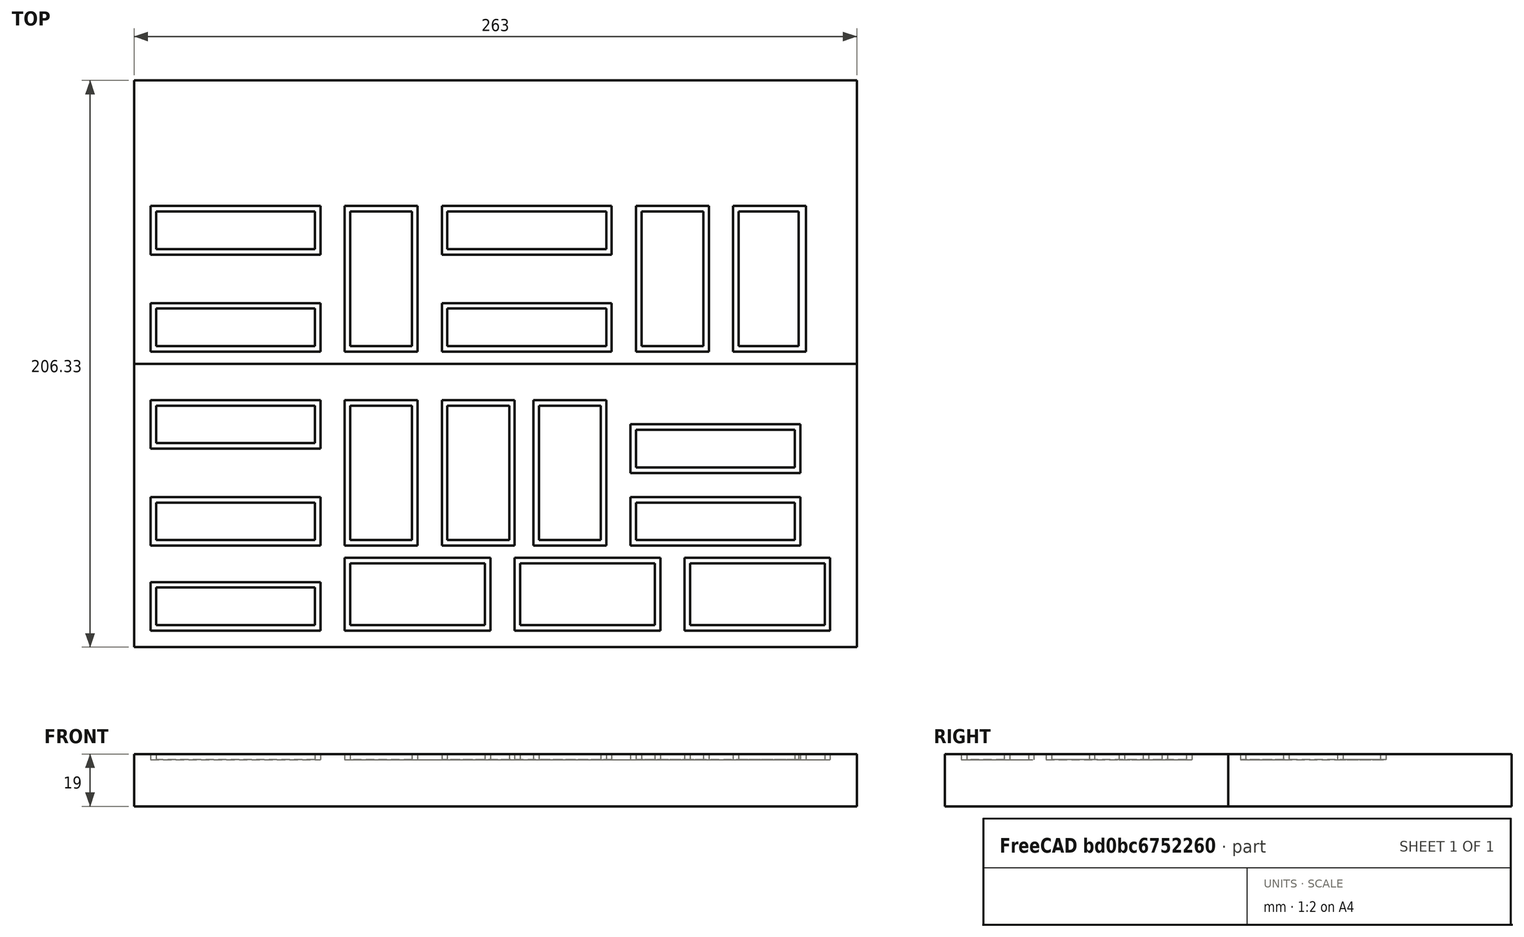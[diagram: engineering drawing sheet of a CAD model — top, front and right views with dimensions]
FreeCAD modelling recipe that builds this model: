
FCSTD DOCUMENT  (FreeCAD 0.22R36958 (Git))
Label: juel_top_3
License: All rights reserved
LicenseURL: http://en.wikipedia.org/wiki/All_rights_reserved
objects: Part::Part2DObjectPython×25, Sketcher::SketchObject×3, PartDesign::Pocket×2, Spreadsheet::Sheet×1, PartDesign::Pad×1, PartDesign::Body×1
note: 35 computed .brp shape members not serialized (recipe doc carries the construction recipe); baked Part::Feature solids carry a one-line shape summary decoded from their .brp

FEATURE [Spreadsheet::Sheet] Spreadsheet  label="vars"
  cells = A1='length; B1(length)=263; C1=263; A2='width; B2(width)==border_size + plot8 * 3 + space_wide + space_narrow * 3; C2=158; A3='height; B3(height)=19; A4='border_size; B4(border_size)=6; A5='cut_height; B5(cut_height)=2; A7='plot10; B7(plot10)==C7 / 20; C7=530; D7=1; A8='plot20; B8(plot20)==C7 / 10; C8=50; D8==200 / E8; E8=5; A9='plot8; B9(plot8)==plot20 / 3; A10='plot25; B10(plot25)==plot10 * 2 + space_narrow; A12='plot border; B12(plot_border)=2; A13='space narrow; B13(space_narrow)==space_wide / 2; A14='space wide; B14(space_wide)==plot20 / 3; A16='font size; B16(font_size)=9.5; A17='x bottom row; B17(x_bottom_row)=-94
FEATURE [Sketcher::SketchObject] Sketch
  AttachmentSupport = -> [XY_Plane]
  FullyConstrained = true
  MapMode = 5
  expr: Constraints[20] = <<vars>>.width
  expr: Constraints[8] = <<vars>>.width
  expr: Constraints[9] = <<vars>>.length
  sketch-geometry (8):
    g0: LineSegment StartX=-131.5 StartY=0 StartZ=0 EndX=131.5 EndY=0 EndZ=0
    g1: LineSegment StartX=131.5 StartY=0 StartZ=0 EndX=131.5 EndY=103.167 EndZ=0
    g2: LineSegment StartX=131.5 StartY=103.167 StartZ=0 EndX=-131.5 EndY=103.167 EndZ=0
    g3: LineSegment StartX=-131.5 StartY=103.167 StartZ=0 EndX=-131.5 EndY=0 EndZ=0
    g4: LineSegment StartX=-131.5 StartY=103.167 StartZ=0 EndX=131.5 EndY=103.167 EndZ=0
    g5: LineSegment StartX=131.5 StartY=103.167 StartZ=0 EndX=131.5 EndY=206.333 EndZ=0
    g6: LineSegment StartX=131.5 StartY=206.333 StartZ=0 EndX=-131.5 EndY=206.333 EndZ=0
    g7: LineSegment StartX=-131.5 StartY=206.333 StartZ=0 EndX=-131.5 EndY=103.167 EndZ=0
  constraints (21):
    c: Coincident(g0,g1)
    c: Coincident(g1,g2)
    c: Coincident(g2,g3)
    c: Coincident(g3,g0)
    c: Horizontal(g0)
    c: Horizontal(g2)
    c: Vertical(g1)
    c: Vertical(g3)
    c: DistanceY(g3,g3) = 103.167
    c: DistanceX(g2,g2) = 263
    c: Symmetric(g0,g0,g-1)
    c: Coincident(g4,g5)
    c: Coincident(g5,g6)
    c: Coincident(g6,g7)
    c: Coincident(g7,g4)
    c: Horizontal(g6)
    c: Vertical(g5)
    c: Vertical(g7)
    c: Coincident(g4,g2)
    c: Coincident(g1,g4)
    c: DistanceY(g7,g7) = 103.167
FEATURE [PartDesign::Pad] Pad
  Direction = (0,0,1)
  Length = 19
  Length2 = 10
  Profile = -> Sketch
  ReferenceAxis = -> Sketch [N_Axis]
  Suppressed = false
  Type = 0
  expr: Length = <<vars>>.height
FEATURE [Sketcher::SketchObject] Sketch001
  AttachmentSupport = -> [Pad]
  ExternalGeometry = -> [Pad]
  FullyConstrained = true
  MapMode = 5
  Placement = pos=(0,0,19) rot=(0,0,1;0rad)
  expr: Constraints[142] = <<vars>>.space_narrow
  expr: Constraints[143] = <<vars>>.space_narrow
  expr: Constraints[144] = <<vars>>.space_narrow
  expr: Constraints[161] = <<vars>>.plot_border
  expr: Constraints[162] = <<vars>>.plot_border
  expr: Constraints[163] = <<vars>>.plot10
  expr: Constraints[164] = <<vars>>.plot_border
  expr: Constraints[165] = <<vars>>.plot_border
  expr: Constraints[166] = <<vars>>.plot20
  expr: Constraints[16] = <<vars>>.plot_border
  expr: Constraints[17] = <<vars>>.plot_border
  expr: Constraints[18] = <<vars>>.plot_border
  expr: Constraints[19] = <<vars>>.plot_border
  expr: Constraints[20] = <<vars>>.plot8
  expr: Constraints[214] = <<vars>>.space_narrow - 2
  expr: Constraints[21] = <<vars>>.plot25
  expr: Constraints[249] = <<vars>>.plot_border
  expr: Constraints[250] = <<vars>>.plot_border
  expr: Constraints[251] = <<vars>>.plot_border
  expr: Constraints[252] = <<vars>>.plot_border
  expr: Constraints[253] = <<vars>>.plot25
  expr: Constraints[254] = <<vars>>.plot25
  expr: Constraints[255] = <<vars>>.plot_border
  expr: Constraints[256] = <<vars>>.plot_border
  expr: Constraints[257] = <<vars>>.plot_border
  expr: Constraints[258] = <<vars>>.plot_border
  expr: Constraints[259] = <<vars>>.plot8
  expr: Constraints[260] = <<vars>>.plot8
  expr: Constraints[263] = <<vars>>.space_narrow
  expr: Constraints[264] = <<vars>>.space_narrow
  expr: Constraints[68] = <<vars>>.border_size
  expr: Constraints[70] = <<vars>>.space_narrow * 1.5
  expr: Constraints[71] = <<vars>>.space_wide
  expr: Constraints[72] = <<vars>>.border_size
  expr: Constraints[89] = <<vars>>.plot_border
  expr: Constraints[90] = <<vars>>.plot_border
  expr: Constraints[91] = <<vars>>.plot_border
  expr: Constraints[92] = <<vars>>.plot_border
  expr: Constraints[93] = <<vars>>.plot10
  expr: Constraints[94] = <<vars>>.plot20
  sketch-geometry (88):
    g0: LineSegment StartX=-125.5 StartY=6 StartZ=0 EndX=-63.6667 EndY=6 EndZ=0
    g1: LineSegment StartX=-63.6667 StartY=6 StartZ=0 EndX=-63.6667 EndY=23.6667 EndZ=0
    g2: LineSegment StartX=-63.6667 StartY=23.6667 StartZ=0 EndX=-125.5 EndY=23.6667 EndZ=0
    g3: LineSegment StartX=-125.5 StartY=23.6667 StartZ=0 EndX=-125.5 EndY=6 EndZ=0
    g4: LineSegment StartX=-65.6667 StartY=21.6667 StartZ=0 EndX=-123.5 EndY=21.6667 EndZ=0
    g5: LineSegment StartX=-123.5 StartY=21.6667 StartZ=0 EndX=-123.5 EndY=8 EndZ=0
    g6: LineSegment StartX=-123.5 StartY=8 StartZ=0 EndX=-65.6667 EndY=8 EndZ=0
    g7: LineSegment StartX=-65.6667 StartY=8 StartZ=0 EndX=-65.6667 EndY=21.6667 EndZ=0
    g8: LineSegment StartX=-125.5 StartY=36.9167 StartZ=0 EndX=-63.6667 EndY=36.9167 EndZ=0
    g9: LineSegment StartX=-63.6667 StartY=36.9167 StartZ=0 EndX=-63.6667 EndY=54.5833 EndZ=0
    g10: LineSegment StartX=-63.6667 StartY=54.5833 StartZ=0 EndX=-125.5 EndY=54.5833 EndZ=0
    g11: LineSegment StartX=-125.5 StartY=54.5833 StartZ=0 EndX=-125.5 EndY=36.9167 EndZ=0
    g12: LineSegment StartX=-65.6667 StartY=52.5833 StartZ=0 EndX=-123.5 EndY=52.5833 EndZ=0
    g13: LineSegment StartX=-123.5 StartY=52.5833 StartZ=0 EndX=-123.5 EndY=38.9167 EndZ=0
    g14: LineSegment StartX=-123.5 StartY=38.9167 StartZ=0 EndX=-65.6667 EndY=38.9167 EndZ=0
    g15: LineSegment StartX=-65.6667 StartY=38.9167 StartZ=0 EndX=-65.6667 EndY=52.5833 EndZ=0
    g16: LineSegment StartX=-125.5 StartY=72.25 StartZ=0 EndX=-63.6667 EndY=72.25 EndZ=0
    g17: LineSegment StartX=-63.6667 StartY=72.25 StartZ=0 EndX=-63.6667 EndY=89.9167 EndZ=0
    g18: LineSegment StartX=-63.6667 StartY=89.9167 StartZ=0 EndX=-125.5 EndY=89.9167 EndZ=0
    g19: LineSegment StartX=-125.5 StartY=89.9167 StartZ=0 EndX=-125.5 EndY=72.25 EndZ=0
    g20: LineSegment StartX=-65.6667 StartY=87.9167 StartZ=0 EndX=-123.5 EndY=87.9167 EndZ=0
    g21: LineSegment StartX=-123.5 StartY=87.9167 StartZ=0 EndX=-123.5 EndY=74.25 EndZ=0
    g22: LineSegment StartX=-123.5 StartY=74.25 StartZ=0 EndX=-65.6667 EndY=74.25 EndZ=0
    g23: LineSegment StartX=-65.6667 StartY=74.25 StartZ=0 EndX=-65.6667 EndY=87.9167 EndZ=0
    g24: LineSegment StartX=-54.8333 StartY=6 StartZ=0 EndX=-1.83333 EndY=6 EndZ=0
    g25: LineSegment StartX=-1.83333 StartY=6 StartZ=0 EndX=-1.83333 EndY=32.5 EndZ=0
    g26: LineSegment StartX=-1.83333 StartY=32.5 StartZ=0 EndX=-54.8333 EndY=32.5 EndZ=0
    g27: LineSegment StartX=-54.8333 StartY=32.5 StartZ=0 EndX=-54.8333 EndY=6 EndZ=0
    g28: LineSegment StartX=-52.8333 StartY=8 StartZ=0 EndX=-3.83333 EndY=8 EndZ=0
    g29: LineSegment StartX=-3.83333 StartY=8 StartZ=0 EndX=-3.83333 EndY=30.5 EndZ=0
    g30: LineSegment StartX=-3.83333 StartY=30.5 StartZ=0 EndX=-52.8333 EndY=30.5 EndZ=0
    g31: LineSegment StartX=-52.8333 StartY=30.5 StartZ=0 EndX=-52.8333 EndY=8 EndZ=0
    g32: LineSegment StartX=7 StartY=6 StartZ=0 EndX=60 EndY=6 EndZ=0
    g33: LineSegment StartX=60 StartY=6 StartZ=0 EndX=60 EndY=32.5 EndZ=0
    g34: LineSegment StartX=60 StartY=32.5 StartZ=0 EndX=7 EndY=32.5 EndZ=0
    g35: LineSegment StartX=7 StartY=32.5 StartZ=0 EndX=7 EndY=6 EndZ=0
    g36: LineSegment StartX=9 StartY=8 StartZ=0 EndX=58 EndY=8 EndZ=0
    g37: LineSegment StartX=58 StartY=8 StartZ=0 EndX=58 EndY=30.5 EndZ=0
    g38: LineSegment StartX=58 StartY=30.5 StartZ=0 EndX=9 EndY=30.5 EndZ=0
    g39: LineSegment StartX=9 StartY=30.5 StartZ=0 EndX=9 EndY=8 EndZ=0
    g40: LineSegment StartX=68.8333 StartY=6 StartZ=0 EndX=121.833 EndY=6 EndZ=0
    g41: LineSegment StartX=121.833 StartY=6 StartZ=0 EndX=121.833 EndY=32.5 EndZ=0
    g42: LineSegment StartX=121.833 StartY=32.5 StartZ=0 EndX=68.8333 EndY=32.5 EndZ=0
    g43: LineSegment StartX=68.8333 StartY=32.5 StartZ=0 EndX=68.8333 EndY=6 EndZ=0
    g44: LineSegment StartX=70.8333 StartY=8 StartZ=0 EndX=119.833 EndY=8 EndZ=0
    g45: LineSegment StartX=119.833 StartY=8 StartZ=0 EndX=119.833 EndY=30.5 EndZ=0
    g46: LineSegment StartX=119.833 StartY=30.5 StartZ=0 EndX=70.8333 EndY=30.5 EndZ=0
    g47: LineSegment StartX=70.8333 StartY=30.5 StartZ=0 EndX=70.8333 EndY=8 EndZ=0
    g48: LineSegment StartX=-54.8333 StartY=36.9167 StartZ=0 EndX=-28.3333 EndY=36.9167 EndZ=0
    g49: LineSegment StartX=-28.3333 StartY=36.9167 StartZ=0 EndX=-28.3333 EndY=89.9167 EndZ=0
    g50: LineSegment StartX=-28.3333 StartY=89.9167 StartZ=0 EndX=-54.8333 EndY=89.9167 EndZ=0
    g51: LineSegment StartX=-54.8333 StartY=89.9167 StartZ=0 EndX=-54.8333 EndY=36.9167 EndZ=0
    g52: LineSegment StartX=-30.3333 StartY=87.9167 StartZ=0 EndX=-52.8333 EndY=87.9167 EndZ=0
    g53: LineSegment StartX=-52.8333 StartY=87.9167 StartZ=0 EndX=-52.8333 EndY=38.9167 EndZ=0
    g54: LineSegment StartX=-52.8333 StartY=38.9167 StartZ=0 EndX=-30.3333 EndY=38.9167 EndZ=0
    g55: LineSegment StartX=-30.3333 StartY=38.9167 StartZ=0 EndX=-30.3333 EndY=87.9167 EndZ=0
    g56: LineSegment StartX=-19.5 StartY=36.9167 StartZ=0 EndX=7 EndY=36.9167 EndZ=0
    g57: LineSegment StartX=7 StartY=36.9167 StartZ=0 EndX=7 EndY=89.9167 EndZ=0
    g58: LineSegment StartX=7 StartY=89.9167 StartZ=0 EndX=-19.5 EndY=89.9167 EndZ=0
    g59: LineSegment StartX=-19.5 StartY=89.9167 StartZ=0 EndX=-19.5 EndY=36.9167 EndZ=0
    g60: LineSegment StartX=5 StartY=87.9167 StartZ=0 EndX=-17.5 EndY=87.9167 EndZ=0
    g61: LineSegment StartX=-17.5 StartY=87.9167 StartZ=0 EndX=-17.5 EndY=38.9167 EndZ=0
    g62: LineSegment StartX=-17.5 StartY=38.9167 StartZ=0 EndX=5 EndY=38.9167 EndZ=0
    g63: LineSegment StartX=5 StartY=38.9167 StartZ=0 EndX=5 EndY=87.9167 EndZ=0
    g64: LineSegment StartX=13.8333 StartY=36.9167 StartZ=0 EndX=40.3333 EndY=36.9167 EndZ=0
    g65: LineSegment StartX=40.3333 StartY=36.9167 StartZ=0 EndX=40.3333 EndY=89.9167 EndZ=0
    g66: LineSegment StartX=40.3333 StartY=89.9167 StartZ=0 EndX=13.8333 EndY=89.9167 EndZ=0
    g67: LineSegment StartX=13.8333 StartY=89.9167 StartZ=0 EndX=13.8333 EndY=36.9167 EndZ=0
    g68: LineSegment StartX=38.3333 StartY=87.9167 StartZ=0 EndX=15.8333 EndY=87.9167 EndZ=0
    g69: LineSegment StartX=15.8333 StartY=87.9167 StartZ=0 EndX=15.8333 EndY=38.9167 EndZ=0
    g70: LineSegment StartX=15.8333 StartY=38.9167 StartZ=0 EndX=38.3333 EndY=38.9167 EndZ=0
    g71: LineSegment StartX=38.3333 StartY=38.9167 StartZ=0 EndX=38.3333 EndY=87.9167 EndZ=0
    g72: LineSegment StartX=49.1667 StartY=36.9167 StartZ=0 EndX=111 EndY=36.9167 EndZ=0
    g73: LineSegment StartX=111 StartY=36.9167 StartZ=0 EndX=111 EndY=54.5833 EndZ=0
    g74: LineSegment StartX=111 StartY=54.5833 StartZ=0 EndX=49.1667 EndY=54.5833 EndZ=0
    g75: LineSegment StartX=49.1667 StartY=54.5833 StartZ=0 EndX=49.1667 EndY=36.9167 EndZ=0
    g76: LineSegment StartX=109 StartY=52.5833 StartZ=0 EndX=51.1667 EndY=52.5833 EndZ=0
    g77: LineSegment StartX=51.1667 StartY=52.5833 StartZ=0 EndX=51.1667 EndY=38.9167 EndZ=0
    g78: LineSegment StartX=51.1667 StartY=38.9167 StartZ=0 EndX=109 EndY=38.9167 EndZ=0
    g79: LineSegment StartX=109 StartY=38.9167 StartZ=0 EndX=109 EndY=52.5833 EndZ=0
    g80: LineSegment StartX=49.1667 StartY=63.4167 StartZ=0 EndX=111 EndY=63.4167 EndZ=0
    g81: LineSegment StartX=111 StartY=63.4167 StartZ=0 EndX=111 EndY=81.0833 EndZ=0
    g82: LineSegment StartX=111 StartY=81.0833 StartZ=0 EndX=49.1667 EndY=81.0833 EndZ=0
    g83: LineSegment StartX=49.1667 StartY=81.0833 StartZ=0 EndX=49.1667 EndY=63.4167 EndZ=0
    g84: LineSegment StartX=109 StartY=79.0833 StartZ=0 EndX=51.1667 EndY=79.0833 EndZ=0
    g85: LineSegment StartX=51.1667 StartY=79.0833 StartZ=0 EndX=51.1667 EndY=65.4167 EndZ=0
    g86: LineSegment StartX=51.1667 StartY=65.4167 StartZ=0 EndX=109 EndY=65.4167 EndZ=0
    g87: LineSegment StartX=109 StartY=65.4167 StartZ=0 EndX=109 EndY=79.0833 EndZ=0
  constraints (265):
    c: Coincident(g0,g1)
    c: Coincident(g1,g2)
    c: Coincident(g2,g3)
    c: Coincident(g3,g0)
    c: Horizontal(g0)
    c: Horizontal(g2)
    c: Vertical(g1)
    c: Vertical(g3)
    c: Coincident(g4,g5)
    c: Coincident(g5,g6)
    c: Coincident(g6,g7)
    c: Coincident(g7,g4)
    c: Horizontal(g4)
    c: Horizontal(g6)
    c: Vertical(g5)
    c: Vertical(g7)
    c: DistanceX(g2,g4) = 2
    c: DistanceY(g4,g2) = 2
    c: DistanceY(g0,g6) = 2
    c: DistanceX(g6,g0) = 2
    c: DistanceY(g1,g1) = 17.6667
    c: DistanceX(g2,g2) = 61.8333
    c: Coincident(g8,g9)
    c: Coincident(g16,g17)
    c: Coincident(g9,g10)
    c: Coincident(g17,g18)
    c: Coincident(g10,g11)
    c: Coincident(g18,g19)
    c: Coincident(g11,g8)
    c: Coincident(g19,g16)
    c: Horizontal(g8)
    c: Horizontal(g16)
    c: Horizontal(g10)
    c: Horizontal(g18)
    c: Vertical(g9)
    c: Vertical(g17)
    c: Vertical(g11)
    c: Vertical(g19)
    c: Coincident(g12,g13)
    c: Coincident(g20,g21)
    c: Coincident(g13,g14)
    c: Coincident(g21,g22)
    c: Coincident(g14,g15)
    c: Coincident(g22,g23)
    c: Coincident(g15,g12)
    c: Coincident(g23,g20)
    c: Horizontal(g12)
    c: Horizontal(g20)
    c: Horizontal(g14)
    c: Horizontal(g22)
    c: Vertical(g13)
    c: Vertical(g21)
    c: Vertical(g15)
    c: Vertical(g23)
    c: DistanceX(g10,g12) = 2
    c: DistanceX(g18,g20) = 2
    c: DistanceY(g12,g10) = 2
    c: DistanceY(g20,g18) = 2
    c: DistanceY(g8,g14) = 2
    c: DistanceY(g16,g22) = 2
    c: DistanceX(g14,g8) = 2
    c: DistanceX(g22,g16) = 2
    c: Equal(g1,g9)
    c: Equal(g1,g17)
    c: Equal(g2,g10)
    c: Equal(g2,g18)
    c: Vertical(g2,g8)
    c: Vertical(g8,g16)
    c: DistanceY(g-3,g0) = 6
    c: Distance(g-3,g0) = 8.48528
    c: DistanceY(g2,g8) = 13.25
    c: DistanceY(g10,g16) = 17.6667
    c: DistanceX(g-3,g0) = 6
    c: Coincident(g24,g25)
    c: Coincident(g25,g26)
    c: Coincident(g26,g27)
    c: Coincident(g27,g24)
    c: Horizontal(g24)
    c: Horizontal(g26)
    c: Vertical(g25)
    c: Vertical(g27)
    c: Coincident(g28,g29)
    c: Coincident(g29,g30)
    c: Coincident(g30,g31)
    c: Coincident(g31,g28)
    c: Horizontal(g28)
    c: Horizontal(g30)
    c: Vertical(g29)
    c: Vertical(g31)
    c: DistanceX(g26,g30) = 2
    c: DistanceX(g28,g24) = 2
    c: DistanceY(g30,g26) = 2
    c: DistanceY(g24,g28) = 2
    c: DistanceY(g27,g27) = 26.5
    c: DistanceX(g26,g26) = 53
    c: Horizontal(g0,g24)
    c: Coincident(g32,g33)
    c: Coincident(g40,g41)
    c: Coincident(g33,g34)
    c: Coincident(g41,g42)
    c: Coincident(g34,g35)
    c: Coincident(g42,g43)
    c: Coincident(g35,g32)
    c: Coincident(g43,g40)
    c: Horizontal(g32)
    c: Horizontal(g40)
    c: Horizontal(g34)
    c: Horizontal(g42)
    c: Vertical(g33)
    c: Vertical(g41)
    c: Vertical(g35)
    c: Vertical(g43)
    c: Coincident(g36,g37)
    c: Coincident(g44,g45)
    c: Coincident(g37,g38)
    c: Coincident(g45,g46)
    c: Coincident(g38,g39)
    c: Coincident(g46,g47)
    c: Coincident(g39,g36)
    c: Coincident(g47,g44)
    c: Horizontal(g36)
    c: Horizontal(g44)
    c: Horizontal(g38)
    c: Horizontal(g46)
    c: Vertical(g37)
    c: Vertical(g45)
    c: Vertical(g39)
    c: Vertical(g47)
    c: DistanceX(g34,g38) = 2
    c: DistanceX(g42,g46) = 2
    c: DistanceX(g36,g32) = 2
    c: DistanceX(g44,g40) = 2
    c: DistanceY(g38,g34) = 2
    c: DistanceY(g46,g42) = 2
    c: DistanceY(g32,g36) = 2
    c: DistanceY(g40,g44) = 2
    c: Equal(g27,g35)
    c: Equal(g27,g43)
    c: Equal(g26,g34)
    c: Equal(g26,g42)
    c: Horizontal(g24,g32)
    c: Horizontal(g32,g40)
    c: DistanceX(g0,g24) = 8.83333
    c: DistanceX(g24,g32) = 8.83333
    c: DistanceX(g32,g40) = 8.83333
    c: Coincident(g48,g49)
    c: Coincident(g49,g50)
    c: Coincident(g50,g51)
    c: Coincident(g51,g48)
    c: Horizontal(g48)
    c: Horizontal(g50)
    c: Vertical(g49)
    c: Vertical(g51)
    c: Coincident(g52,g53)
    c: Coincident(g53,g54)
    c: Coincident(g54,g55)
    c: Coincident(g55,g52)
    c: Horizontal(g52)
    c: Horizontal(g54)
    c: Vertical(g53)
    c: Vertical(g55)
    c: DistanceX(g50,g52) = 2
    c: DistanceX(g54,g48) = 2
    c: DistanceX(g48,g48) = 26.5
    c: DistanceY(g52,g50) = 2
    c: DistanceY(g48,g54) = 2
    c: DistanceY(g49,g49) = 53
    c: Horizontal(g8,g48)
    c: Coincident(g56,g57)
    c: Coincident(g64,g65)
    c: Coincident(g57,g58)
    c: Coincident(g65,g66)
    c: Coincident(g58,g59)
    c: Coincident(g66,g67)
    c: Coincident(g59,g56)
    c: Coincident(g67,g64)
    c: Horizontal(g56)
    c: Horizontal(g64)
    c: Horizontal(g58)
    c: Horizontal(g66)
    c: Vertical(g57)
    c: Vertical(g65)
    c: Vertical(g59)
    c: Vertical(g67)
    c: Coincident(g60,g61)
    c: Coincident(g68,g69)
    c: Coincident(g61,g62)
    c: Coincident(g69,g70)
    c: Coincident(g62,g63)
    c: Coincident(g70,g71)
    c: Coincident(g63,g60)
    c: Coincident(g71,g68)
    c: Horizontal(g60)
    c: Horizontal(g68)
    c: Horizontal(g62)
    c: Horizontal(g70)
    c: Vertical(g61)
    c: Vertical(g69)
    c: Vertical(g63)
    c: Vertical(g71)
    c: DistanceX(g58,g60) = 2
    c: DistanceX(g66,g68) = 2
    c: DistanceX(g62,g56) = 2
    c: DistanceX(g70,g64) = 2
    c: Equal(g48,g56)
    c: Equal(g48,g64)
    c: DistanceY(g60,g58) = 2
    c: DistanceY(g68,g66) = 2
    c: DistanceY(g56,g62) = 2
    c: DistanceY(g64,g70) = 2
    c: Equal(g49,g57)
    c: Equal(g49,g65)
    c: Vertical(g26,g48)
    c: Vertical(g56,g34)
    c: DistanceX(g56,g64) = 6.83333
    c: Horizontal(g48,g56)
    c: Horizontal(g56,g64)
    c: Coincident(g72,g73)
    c: Coincident(g73,g74)
    c: Coincident(g74,g75)
    c: Coincident(g75,g72)
    c: Horizontal(g72)
    c: Horizontal(g74)
    c: Vertical(g73)
    c: Vertical(g75)
    c: Coincident(g76,g77)
    c: Coincident(g77,g78)
    c: Coincident(g78,g79)
    c: Coincident(g79,g76)
    c: Horizontal(g76)
    c: Horizontal(g78)
    c: Vertical(g77)
    c: Vertical(g79)
    c: Coincident(g80,g81)
    c: Coincident(g81,g82)
    c: Coincident(g82,g83)
    c: Coincident(g83,g80)
    c: Horizontal(g80)
    c: Horizontal(g82)
    c: Vertical(g81)
    c: Vertical(g83)
    c: Coincident(g84,g85)
    c: Coincident(g85,g86)
    c: Coincident(g86,g87)
    c: Coincident(g87,g84)
    c: Horizontal(g84)
    c: Horizontal(g86)
    c: Vertical(g85)
    c: Vertical(g87)
    c: DistanceX(g82,g84) = 2
    c: DistanceX(g86,g80) = 2
    c: DistanceX(g74,g76) = 2
    c: DistanceX(g78,g72) = 2
    c: DistanceX(g74,g74) = 61.8333
    c: DistanceX(g82,g82) = 61.8333
    c: DistanceY(g84,g82) = 2
    c: DistanceY(g80,g86) = 2
    c: DistanceY(g76,g74) = 2
    c: DistanceY(g72,g78) = 2
    c: DistanceY(g73,g73) = 17.6667
    c: DistanceY(g81,g81) = 17.6667
    c: Vertical(g74,g80)
    c: Horizontal(g64,g72)
    c: DistanceX(g64,g72) = 8.83333
    c: DistanceY(g74,g80) = 8.83333
FEATURE [PartDesign::Pocket] Pocket
  BaseFeature = -> Pad
  Direction = (0,0,-1)
  Length = 2
  Length2 = 5
  Profile = -> Sketch001
  ReferenceAxis = -> Sketch001 [N_Axis]
  Suppressed = false
  Type = 0
  expr: Length = <<vars>>.cut_height
FEATURE [Part::Part2DObjectPython] ShapeString  label="18"  # Draft 2D object (typed FeaturePython)
  FontFile = /System/Library/Fonts/Avenir Next Condensed.ttc
  Fuse = false
  Justification = 4
  JustificationReference = 0
  KeepLeftMargin = false
  MakeFace = true
  ObliqueAngle = 0
  Placement = pos=(-94,14.7,19.01) rot=(0,0,1;4.71239rad)
  ScaleToSize = true
  Size = 9.5
  String = 18
  Tracking = 0
  expr: .Placement.Base.x = <<vars>>.x_bottom_row
  expr: Size = <<vars>>.font_size
FEATURE [Sketcher::SketchObject] Sketch002
  AttachmentSupport = -> [Pocket]
  ExternalGeometry = -> [Pocket]
  FullyConstrained = true
  MapMode = 5
  Placement = pos=(0,0,19) rot=(0,0,1;0rad)
  expr: Constraints[112] = <<vars>>.plot_border
  expr: Constraints[113] = <<vars>>.plot_border
  expr: Constraints[114] = <<vars>>.plot_border
  expr: Constraints[115] = <<vars>>.plot_border
  expr: Constraints[116] = <<vars>>.plot_border
  expr: Constraints[117] = <<vars>>.plot_border
  expr: Constraints[118] = <<vars>>.plot_border
  expr: Constraints[119] = <<vars>>.plot_border
  expr: Constraints[120] = <<vars>>.plot_border
  expr: Constraints[121] = <<vars>>.plot_border
  expr: Constraints[122] = <<vars>>.plot_border
  expr: Constraints[123] = <<vars>>.plot_border
  expr: Constraints[124] = <<vars>>.plot_border
  expr: Constraints[126] = <<vars>>.plot_border
  expr: Constraints[127] = <<vars>>.plot_border
  expr: Constraints[128] = <<vars>>.plot_border
  expr: Constraints[129] = <<vars>>.plot_border
  expr: Constraints[130] = <<vars>>.plot_border
  expr: Constraints[131] = <<vars>>.plot_border
  expr: Constraints[132] = <<vars>>.plot_border
  expr: Constraints[133] = <<vars>>.plot_border
  expr: Constraints[134] = <<vars>>.plot_border
  expr: Constraints[135] = <<vars>>.plot_border
  expr: Constraints[136] = <<vars>>.plot_border
  expr: Constraints[137] = <<vars>>.plot_border
  expr: Constraints[138] = <<vars>>.plot_border
  expr: Constraints[139] = <<vars>>.plot_border
  expr: Constraints[140] = <<vars>>.plot20
  expr: Constraints[141] = <<vars>>.plot20
  expr: Constraints[142] = <<vars>>.plot8
  expr: Constraints[143] = <<vars>>.plot8
  expr: Constraints[144] = <<vars>>.plot20
  expr: Constraints[145] = <<vars>>.plot8
  expr: Constraints[146] = <<vars>>.plot8
  expr: Constraints[147] = <<vars>>.plot25
  expr: Constraints[148] = <<vars>>.plot25
  expr: Constraints[149] = <<vars>>.plot10
  expr: Constraints[150] = <<vars>>.plot25
  expr: Constraints[151] = <<vars>>.plot25
  expr: Constraints[152] = <<vars>>.plot10
  expr: Constraints[153] = <<vars>>.plot10
  expr: Constraints[154] = <<vars>>.space_narrow / 2
  expr: Constraints[155] = <<vars>>.border_size
  expr: Constraints[164] = <<vars>>.space_narrow
  expr: Constraints[165] = <<vars>>.space_narrow
  expr: Constraints[166] = <<vars>>.space_narrow
  expr: Constraints[167] = <<vars>>.space_narrow
  sketch-geometry (56):
    g0: LineSegment StartX=-125.5 StartY=107.583 StartZ=0 EndX=-63.6667 EndY=107.583 EndZ=0
    g1: LineSegment StartX=-63.6667 StartY=107.583 StartZ=0 EndX=-63.6667 EndY=125.25 EndZ=0
    g2: LineSegment StartX=-63.6667 StartY=125.25 StartZ=0 EndX=-125.5 EndY=125.25 EndZ=0
    g3: LineSegment StartX=-125.5 StartY=125.25 StartZ=0 EndX=-125.5 EndY=107.583 EndZ=0
    g4: LineSegment StartX=-65.6667 StartY=123.25 StartZ=0 EndX=-123.5 EndY=123.25 EndZ=0
    g5: LineSegment StartX=-123.5 StartY=123.25 StartZ=0 EndX=-123.5 EndY=109.583 EndZ=0
    g6: LineSegment StartX=-123.5 StartY=109.583 StartZ=0 EndX=-65.6667 EndY=109.583 EndZ=0
    g7: LineSegment StartX=-65.6667 StartY=109.583 StartZ=0 EndX=-65.6667 EndY=123.25 EndZ=0
    g8: LineSegment StartX=-125.5 StartY=142.917 StartZ=0 EndX=-63.6667 EndY=142.917 EndZ=0
    g9: LineSegment StartX=-63.6667 StartY=142.917 StartZ=0 EndX=-63.6667 EndY=160.583 EndZ=0
    g10: LineSegment StartX=-63.6667 StartY=160.583 StartZ=0 EndX=-125.5 EndY=160.583 EndZ=0
    g11: LineSegment StartX=-125.5 StartY=160.583 StartZ=0 EndX=-125.5 EndY=142.917 EndZ=0
    g12: LineSegment StartX=-65.6667 StartY=158.583 StartZ=0 EndX=-123.5 EndY=158.583 EndZ=0
    g13: LineSegment StartX=-123.5 StartY=158.583 StartZ=0 EndX=-123.5 EndY=144.917 EndZ=0
    g14: LineSegment StartX=-123.5 StartY=144.917 StartZ=0 EndX=-65.6667 EndY=144.917 EndZ=0
    g15: LineSegment StartX=-65.6667 StartY=144.917 StartZ=0 EndX=-65.6667 EndY=158.583 EndZ=0
    g16: LineSegment StartX=-54.8333 StartY=160.583 StartZ=0 EndX=-54.8333 EndY=107.583 EndZ=0
    g17: LineSegment StartX=-54.8333 StartY=107.583 StartZ=0 EndX=-28.3333 EndY=107.583 EndZ=0
    g18: LineSegment StartX=-28.3333 StartY=107.583 StartZ=0 EndX=-28.3333 EndY=160.583 EndZ=0
    g19: LineSegment StartX=-28.3333 StartY=160.583 StartZ=0 EndX=-54.8333 EndY=160.583 EndZ=0
    g20: LineSegment StartX=-30.3333 StartY=109.583 StartZ=0 EndX=-30.3333 EndY=158.583 EndZ=0
    g21: LineSegment StartX=-30.3333 StartY=158.583 StartZ=0 EndX=-52.8333 EndY=158.583 EndZ=0
    g22: LineSegment StartX=-52.8333 StartY=158.583 StartZ=0 EndX=-52.8333 EndY=109.583 EndZ=0
    g23: LineSegment StartX=-52.8333 StartY=109.583 StartZ=0 EndX=-30.3333 EndY=109.583 EndZ=0
    g24: LineSegment StartX=42.3333 StartY=125.25 StartZ=0 EndX=-19.5 EndY=125.25 EndZ=0
    g25: LineSegment StartX=-19.5 StartY=125.25 StartZ=0 EndX=-19.5 EndY=107.583 EndZ=0
    g26: LineSegment StartX=-19.5 StartY=107.583 StartZ=0 EndX=42.3333 EndY=107.583 EndZ=0
    g27: LineSegment StartX=42.3333 StartY=107.583 StartZ=0 EndX=42.3333 EndY=125.25 EndZ=0
    g28: LineSegment StartX=-17.5 StartY=109.583 StartZ=0 EndX=40.3333 EndY=109.583 EndZ=0
    g29: LineSegment StartX=40.3333 StartY=109.583 StartZ=0 EndX=40.3333 EndY=123.25 EndZ=0
    g30: LineSegment StartX=40.3333 StartY=123.25 StartZ=0 EndX=-17.5 EndY=123.25 EndZ=0
    g31: LineSegment StartX=-17.5 StartY=123.25 StartZ=0 EndX=-17.5 EndY=109.583 EndZ=0
    g32: LineSegment StartX=51.1667 StartY=160.583 StartZ=0 EndX=51.1667 EndY=107.583 EndZ=0
    g33: LineSegment StartX=51.1667 StartY=107.583 StartZ=0 EndX=77.6667 EndY=107.583 EndZ=0
    g34: LineSegment StartX=77.6667 StartY=107.583 StartZ=0 EndX=77.6667 EndY=160.583 EndZ=0
    g35: LineSegment StartX=77.6667 StartY=160.583 StartZ=0 EndX=51.1667 EndY=160.583 EndZ=0
    g36: LineSegment StartX=75.6667 StartY=109.583 StartZ=0 EndX=75.6667 EndY=158.583 EndZ=0
    g37: LineSegment StartX=75.6667 StartY=158.583 StartZ=0 EndX=53.1667 EndY=158.583 EndZ=0
    g38: LineSegment StartX=53.1667 StartY=158.583 StartZ=0 EndX=53.1667 EndY=109.583 EndZ=0
    g39: LineSegment StartX=53.1667 StartY=109.583 StartZ=0 EndX=75.6667 EndY=109.583 EndZ=0
    g40: LineSegment StartX=86.5 StartY=160.583 StartZ=0 EndX=86.5 EndY=107.583 EndZ=0
    g41: LineSegment StartX=86.5 StartY=107.583 StartZ=0 EndX=113 EndY=107.583 EndZ=0
    g42: LineSegment StartX=113 StartY=107.583 StartZ=0 EndX=113 EndY=160.583 EndZ=0
    g43: LineSegment StartX=113 StartY=160.583 StartZ=0 EndX=86.5 EndY=160.583 EndZ=0
    g44: LineSegment StartX=110.32 StartY=109.583 StartZ=0 EndX=110.32 EndY=158.583 EndZ=0
    g45: LineSegment StartX=110.32 StartY=158.583 StartZ=0 EndX=88.5 EndY=158.583 EndZ=0
    g46: LineSegment StartX=88.5 StartY=158.583 StartZ=0 EndX=88.5 EndY=109.583 EndZ=0
    g47: LineSegment StartX=88.5 StartY=109.583 StartZ=0 EndX=110.32 EndY=109.583 EndZ=0
    g48: LineSegment StartX=-19.5 StartY=160.583 StartZ=0 EndX=-19.5 EndY=142.917 EndZ=0
    g49: LineSegment StartX=-19.5 StartY=142.917 StartZ=0 EndX=42.3333 EndY=142.917 EndZ=0
    g50: LineSegment StartX=42.3333 StartY=142.917 StartZ=0 EndX=42.3333 EndY=160.583 EndZ=0
    g51: LineSegment StartX=42.3333 StartY=160.583 StartZ=0 EndX=-19.5 EndY=160.583 EndZ=0
    g52: LineSegment StartX=40.3333 StartY=144.917 StartZ=0 EndX=40.3333 EndY=158.583 EndZ=0
    g53: LineSegment StartX=40.3333 StartY=158.583 StartZ=0 EndX=-17.5 EndY=158.583 EndZ=0
    g54: LineSegment StartX=-17.5 StartY=158.583 StartZ=0 EndX=-17.5 EndY=144.917 EndZ=0
    g55: LineSegment StartX=-17.5 StartY=144.917 StartZ=0 EndX=40.3333 EndY=144.917 EndZ=0
  constraints (168):
    c: Coincident(g0,g1)
    c: Coincident(g1,g2)
    c: Coincident(g2,g3)
    c: Coincident(g3,g0)
    c: Horizontal(g0)
    c: Horizontal(g2)
    c: Vertical(g1)
    c: Vertical(g3)
    c: Coincident(g4,g5)
    c: Coincident(g5,g6)
    c: Coincident(g6,g7)
    c: Coincident(g7,g4)
    c: Horizontal(g4)
    c: Horizontal(g6)
    c: Vertical(g5)
    c: Vertical(g7)
    c: Coincident(g8,g9)
    c: Coincident(g9,g10)
    c: Coincident(g10,g11)
    c: Coincident(g11,g8)
    c: Horizontal(g8)
    c: Horizontal(g10)
    c: Vertical(g9)
    c: Vertical(g11)
    c: Coincident(g12,g13)
    c: Coincident(g13,g14)
    c: Coincident(g14,g15)
    c: Coincident(g15,g12)
    c: Horizontal(g12)
    c: Horizontal(g14)
    c: Vertical(g13)
    c: Vertical(g15)
    c: Coincident(g16,g17)
    c: Coincident(g17,g18)
    c: Coincident(g18,g19)
    c: Coincident(g19,g16)
    c: Vertical(g16)
    c: Vertical(g18)
    c: Horizontal(g17)
    c: Horizontal(g19)
    c: Coincident(g20,g21)
    c: Coincident(g21,g22)
    c: Coincident(g22,g23)
    c: Coincident(g23,g20)
    c: Vertical(g20)
    c: Vertical(g22)
    c: Horizontal(g21)
    c: Horizontal(g23)
    c: Coincident(g24,g25)
    c: Coincident(g25,g26)
    c: Coincident(g26,g27)
    c: Coincident(g27,g24)
    c: Horizontal(g24)
    c: Horizontal(g26)
    c: Vertical(g25)
    c: Vertical(g27)
    c: Coincident(g28,g29)
    c: Coincident(g29,g30)
    c: Coincident(g30,g31)
    c: Coincident(g31,g28)
    c: Horizontal(g28)
    c: Horizontal(g30)
    c: Vertical(g29)
    c: Vertical(g31)
    c: Coincident(g32,g33)
    c: Coincident(g33,g34)
    c: Coincident(g34,g35)
    c: Coincident(g35,g32)
    c: Vertical(g32)
    c: Vertical(g34)
    c: Horizontal(g33)
    c: Horizontal(g35)
    c: Coincident(g36,g37)
    c: Coincident(g37,g38)
    c: Coincident(g38,g39)
    c: Coincident(g39,g36)
    c: Vertical(g36)
    c: Vertical(g38)
    c: Horizontal(g37)
    c: Horizontal(g39)
    c: Coincident(g40,g41)
    c: Coincident(g41,g42)
    c: Coincident(g42,g43)
    c: Coincident(g43,g40)
    c: Vertical(g40)
    c: Vertical(g42)
    c: Horizontal(g41)
    c: Horizontal(g43)
    c: Coincident(g44,g45)
    c: Coincident(g45,g46)
    c: Coincident(g46,g47)
    c: Coincident(g47,g44)
    c: Vertical(g44)
    c: Vertical(g46)
    c: Horizontal(g45)
    c: Horizontal(g47)
    c: Coincident(g48,g49)
    c: Coincident(g49,g50)
    c: Coincident(g50,g51)
    c: Coincident(g51,g48)
    c: Vertical(g48)
    c: Vertical(g50)
    c: Horizontal(g49)
    c: Horizontal(g51)
    c: Coincident(g52,g53)
    c: Coincident(g53,g54)
    c: Coincident(g54,g55)
    c: Coincident(g55,g52)
    c: Vertical(g52)
    c: Vertical(g54)
    c: Horizontal(g53)
    c: Horizontal(g55)
    c: DistanceX(g10,g12) = 2
    c: DistanceX(g2,g4) = 2
    c: DistanceX(g6,g0) = 2
    c: DistanceX(g14,g8) = 2
    c: DistanceX(g16,g21) = 2
    c: DistanceX(g20,g17) = 2
    c: DistanceX(g24,g30) = 2
    c: DistanceX(g48,g53) = 2
    c: DistanceX(g52,g49) = 2
    c: DistanceX(g28,g26) = 2
    c: DistanceX(g32,g37) = 2
    c: DistanceX(g36,g33) = 2
    c: DistanceX(g40,g45) = 2
    c: DistanceX(g44,g41) = 2.68
    c: DistanceY(g12,g10) = 2
    c: DistanceY(g4,g2) = 2
    c: DistanceY(g0,g6) = 2
    c: DistanceY(g8,g14) = 2
    c: DistanceY(g21,g16) = 2
    c: DistanceY(g17,g20) = 2
    c: DistanceY(g53,g48) = 2
    c: DistanceY(g30,g24) = 2
    c: DistanceY(g26,g28) = 2
    c: DistanceY(g49,g52) = 2
    c: DistanceY(g37,g32) = 2
    c: DistanceY(g33,g36) = 2
    c: DistanceY(g41,g44) = 2
    c: DistanceY(g45,g40) = 2
    c: DistanceY(g40,g40) = 53
    c: DistanceY(g32,g32) = 53
    c: DistanceY(g25,g25) = 17.6667
    c: DistanceY(g48,g48) = 17.6667
    c: DistanceY(g16,g16) = 53
    c: DistanceY(g11,g11) = 17.6667
    c: DistanceY(g3,g3) = 17.6667
    c: DistanceX(g10,g10) = 61.8333
    c: DistanceX(g2,g2) = 61.8333
    c: DistanceX(g19,g19) = 26.5
    c: DistanceX(g51,g51) = 61.8333
    c: DistanceX(g24,g24) = 61.8333
    c: DistanceX(g35,g35) = 26.5
    c: DistanceX(g43,g43) = 26.5
    c: DistanceY(g-6,g0) = 4.41667
    c: DistanceX(g-6,g0) = 6
    c: Vertical(g8,g2)
    c: Vertical(g24,g48)
    c: Horizontal(g0,g16)
    c: Horizontal(g9,g16)
    c: Horizontal(g17,g25)
    c: Horizontal(g18,g48)
    c: Horizontal(g50,g32)
    c: Horizontal(g34,g40)
    c: DistanceX(g0,g16) = 8.83333
    c: DistanceX(g17,g25) = 8.83333
    c: DistanceX(g26,g32) = 8.83333
    c: DistanceX(g33,g40) = 8.83333
FEATURE [PartDesign::Pocket] Pocket001
  BaseFeature = -> Pocket
  Direction = (0,0,-1)
  Length = 2
  Length2 = 5
  Profile = -> Sketch002
  ReferenceAxis = -> Sketch002 [N_Axis]
  Suppressed = false
  Type = 0
  expr: Length = <<vars>>.cut_height
FEATURE [PartDesign::Body] Body
  Group = -> [Sketch,Pad,Sketch001,Pocket,Sketch002,Pocket001]
  Origin = -> Origin
  Tip = -> Pocket001
FEATURE [Part::Part2DObjectPython] ShapeString001  label="14"  # Draft 2D object (typed FeaturePython)
  FontFile = /System/Library/Fonts/Avenir Next Condensed.ttc
  Fuse = false
  Justification = 4
  JustificationReference = 0
  KeepLeftMargin = false
  MakeFace = true
  ObliqueAngle = 0
  Placement = pos=(-94,45.79,19.01) rot=(0,0,1;4.71239rad)
  ScaleToSize = true
  Size = 9.5
  String = 14
  Tracking = 0
  expr: .Placement.Base.x = <<vars>>.x_bottom_row
  expr: Size = <<vars>>.font_size
FEATURE [Part::Part2DObjectPython] ShapeString002  label="13"  # Draft 2D object (typed FeaturePython)
  FontFile = /System/Library/Fonts/Avenir Next Condensed.ttc
  Fuse = false
  Justification = 4
  JustificationReference = 0
  KeepLeftMargin = false
  MakeFace = true
  ObliqueAngle = 0
  Placement = pos=(-94,81,19.1) rot=(0,0,1;4.71239rad)
  ScaleToSize = true
  Size = 9.5
  String = 13
  Tracking = 0
  expr: .Placement.Base.x = <<vars>>.x_bottom_row
  expr: Size = <<vars>>.font_size
FEATURE [Part::Part2DObjectPython] ShapeString003  label="7"  # Draft 2D object (typed FeaturePython)
  FontFile = /System/Library/Fonts/Avenir Next Condensed.ttc
  Fuse = false
  Justification = 4
  JustificationReference = 0
  KeepLeftMargin = false
  MakeFace = true
  ObliqueAngle = 0
  Placement = pos=(-94,116,19.01) rot=(0,0,1;4.71239rad)
  ScaleToSize = true
  Size = 9.5
  String = 7
  Tracking = 0
  expr: .Placement.Base.x = <<vars>>.x_bottom_row
  expr: Size = <<vars>>.font_size
FEATURE [Part::Part2DObjectPython] ShapeString004  label="6"  # Draft 2D object (typed FeaturePython)
  FontFile = /System/Library/Fonts/Avenir Next Condensed.ttc
  Fuse = false
  Justification = 4
  JustificationReference = 0
  KeepLeftMargin = false
  MakeFace = true
  ObliqueAngle = 0
  Placement = pos=(-94,151,19.01) rot=(0,0,1;4.71239rad)
  ScaleToSize = true
  Size = 9.5
  String = 6
  Tracking = 0
  expr: .Placement.Base.x = <<vars>>.x_bottom_row
  expr: Size = <<vars>>.font_size
FEATURE [Part::Part2DObjectPython] ShapeString005  label="5"  # Draft 2D object (typed FeaturePython)
  FontFile = /System/Library/Fonts/Avenir Next Condensed.ttc
  Fuse = false
  Justification = 6
  JustificationReference = 0
  KeepLeftMargin = false
  MakeFace = true
  ObliqueAngle = 0
  Placement = pos=(-46,138,19.01) rot=(0,0,1;4.71239rad)
  ScaleToSize = true
  Size = 9.5
  String = 5
  Tracking = 0
  expr: Size = <<vars>>.font_size
FEATURE [Part::Part2DObjectPython] ShapeString006  label="4"  # Draft 2D object (typed FeaturePython)
  FontFile = /System/Library/Fonts/Avenir Next Condensed.ttc
  Fuse = false
  Justification = 4
  JustificationReference = 0
  KeepLeftMargin = false
  MakeFace = true
  ObliqueAngle = 0
  Placement = pos=(11,116,19.01) rot=(0,0,1;4.71239rad)
  ScaleToSize = true
  Size = 9.5
  String = 4
  Tracking = 0
  expr: Size = <<vars>>.font_size
FEATURE [Part::Part2DObjectPython] ShapeString007  label="3"  # Draft 2D object (typed FeaturePython)
  FontFile = /System/Library/Fonts/Avenir Next Condensed.ttc
  Fuse = false
  Justification = 4
  JustificationReference = 0
  KeepLeftMargin = false
  MakeFace = true
  ObliqueAngle = 0
  Placement = pos=(11,151,19.01) rot=(0,0,1;4.71239rad)
  ScaleToSize = true
  Size = 9.5
  String = 3
  Tracking = 0
  expr: Size = <<vars>>.font_size
FEATURE [Part::Part2DObjectPython] ShapeString008  label="2"  # Draft 2D object (typed FeaturePython)
  FontFile = /System/Library/Fonts/Avenir Next Condensed.ttc
  Fuse = false
  Justification = 4
  JustificationReference = 0
  KeepLeftMargin = false
  MakeFace = true
  ObliqueAngle = 0
  Placement = pos=(65,134,19.01) rot=(0,0,1;4.71239rad)
  ScaleToSize = true
  Size = 9.5
  String = 2
  Tracking = 0
  expr: Size = <<vars>>.font_size
FEATURE [Part::Part2DObjectPython] ShapeString009  label="1"  # Draft 2D object (typed FeaturePython)
  FontFile = /System/Library/Fonts/Avenir Next Condensed.ttc
  Fuse = false
  Justification = 6
  JustificationReference = 0
  KeepLeftMargin = false
  MakeFace = true
  ObliqueAngle = 0
  Placement = pos=(94,137,19.01) rot=(0,0,1;4.71239rad)
  ScaleToSize = true
  Size = 9.5
  String = 1
  Tracking = 0
  expr: Size = <<vars>>.font_size
FEATURE [Part::Part2DObjectPython] ShapeString010  label="8"  # Draft 2D object (typed FeaturePython)
  FontFile = /System/Library/Fonts/Avenir Next Condensed.ttc
  Fuse = false
  Justification = 4
  JustificationReference = 0
  KeepLeftMargin = false
  MakeFace = true
  ObliqueAngle = 0
  Placement = pos=(80,72,19.01) rot=(0,0,1;4.71239rad)
  ScaleToSize = true
  Size = 9.5
  String = 8
  Tracking = 0
  expr: Size = <<vars>>.font_size
FEATURE [Part::Part2DObjectPython] ShapeString011  label="9"  # Draft 2D object (typed FeaturePython)
  FontFile = /System/Library/Fonts/Avenir Next Condensed.ttc
  Fuse = false
  Justification = 4
  JustificationReference = 0
  KeepLeftMargin = false
  MakeFace = true
  ObliqueAngle = 0
  Placement = pos=(80,45,19.01) rot=(0,0,1;4.71239rad)
  ScaleToSize = true
  Size = 9.5
  String = 9
  Tracking = 0
  expr: Size = <<vars>>.font_size
FEATURE [Part::Part2DObjectPython] ShapeString012  label="10"  # Draft 2D object (typed FeaturePython)
  FontFile = /System/Library/Fonts/Avenir Next Condensed.ttc
  Fuse = false
  Justification = 4
  JustificationReference = 0
  KeepLeftMargin = false
  MakeFace = true
  ObliqueAngle = 0
  Placement = pos=(27,63,19.01) rot=(0,0,1;4.71239rad)
  ScaleToSize = true
  Size = 9.5
  String = 10
  Tracking = 0
  expr: Size = <<vars>>.font_size
FEATURE [Part::Part2DObjectPython] ShapeString013  label="11"  # Draft 2D object (typed FeaturePython)
  FontFile = /System/Library/Fonts/Avenir Next Condensed.ttc
  Fuse = false
  Justification = 4
  JustificationReference = 0
  KeepLeftMargin = false
  MakeFace = true
  ObliqueAngle = 0
  Placement = pos=(-6,63,19.01) rot=(0,0,1;4.71239rad)
  ScaleToSize = true
  Size = 9.5
  String = 11
  Tracking = 0
  expr: Size = <<vars>>.font_size
FEATURE [Part::Part2DObjectPython] ShapeString014  label="12"  # Draft 2D object (typed FeaturePython)
  FontFile = /System/Library/Fonts/Avenir Next Condensed.ttc
  Fuse = false
  Justification = 4
  JustificationReference = 0
  KeepLeftMargin = false
  MakeFace = true
  ObliqueAngle = 0
  Placement = pos=(-41,62,19.01) rot=(0,0,1;4.71239rad)
  ScaleToSize = true
  Size = 9.5
  String = 12
  Tracking = 0
  expr: Size = <<vars>>.font_size
FEATURE [Part::Part2DObjectPython] ShapeString015  label="15"  # Draft 2D object (typed FeaturePython)
  FontFile = /System/Library/Fonts/Avenir Next Condensed.ttc
  Fuse = false
  Justification = 4
  JustificationReference = 0
  KeepLeftMargin = false
  MakeFace = true
  ObliqueAngle = 0
  Placement = pos=(94.73,19.55,19.01) rot=(0,0,1;4.71239rad)
  ScaleToSize = true
  Size = 9.5
  String = 15
  Tracking = 0
  expr: Size = <<vars>>.font_size
FEATURE [Part::Part2DObjectPython] ShapeString016  label="16"  # Draft 2D object (typed FeaturePython)
  FontFile = /System/Library/Fonts/Avenir Next Condensed.ttc
  Fuse = false
  Justification = 4
  JustificationReference = 0
  KeepLeftMargin = false
  MakeFace = true
  ObliqueAngle = 0
  Placement = pos=(32,19,19.01) rot=(0,0,1;4.71239rad)
  ScaleToSize = true
  Size = 9.5
  String = 16
  Tracking = 0
  expr: Size = <<vars>>.font_size
FEATURE [Part::Part2DObjectPython] ShapeString017  label="17"  # Draft 2D object (typed FeaturePython)
  FontFile = /System/Library/Fonts/Avenir Next Condensed.ttc
  Fuse = false
  Justification = 4
  JustificationReference = 0
  KeepLeftMargin = false
  MakeFace = true
  ObliqueAngle = 0
  Placement = pos=(-28,19,19.01) rot=(0,0,1;4.71239rad)
  ScaleToSize = true
  Size = 9.5
  String = 17
  Tracking = 0
  expr: Size = <<vars>>.font_size
FEATURE [Part::Part2DObjectPython] ShapeString018  label="P"  # Draft 2D object (typed FeaturePython)
  FontFile = /System/Library/Fonts/Avenir Next Condensed.ttc
  Fuse = false
  Justification = 4
  JustificationReference = 0
  KeepLeftMargin = false
  MakeFace = true
  ObliqueAngle = 0
  Placement = pos=(106,186,19.01) rot=(0,0,1;4.71239rad)
  ScaleToSize = true
  Size = 28.5
  String = P
  Tracking = 0
  expr: Size = <<vars>>.font_size * 3
FEATURE [Part::Part2DObjectPython] ShapeString019  label="L"  # Draft 2D object (typed FeaturePython)
  FontFile = /System/Library/Fonts/Avenir Next Condensed.ttc
  Fuse = false
  Justification = 4
  JustificationReference = 0
  KeepLeftMargin = false
  MakeFace = true
  ObliqueAngle = 0
  Placement = pos=(72,188,19.01) rot=(0,0,1;4.71239rad)
  ScaleToSize = true
  Size = 28.5
  String = L
  Tracking = 0
  expr: Size = <<vars>>.font_size * 3
FEATURE [Part::Part2DObjectPython] ShapeString020  label="O"  # Draft 2D object (typed FeaturePython)
  FontFile = /System/Library/Fonts/Avenir Next Condensed.ttc
  Fuse = false
  Justification = 4
  JustificationReference = 0
  KeepLeftMargin = false
  MakeFace = true
  ObliqueAngle = 0
  Placement = pos=(37,187,20.01) rot=(0,0,1;4.71239rad)
  ScaleToSize = true
  Size = 28.5
  String = O
  Tracking = 0
  expr: Size = <<vars>>.font_size * 3
FEATURE [Part::Part2DObjectPython] ShapeString021  label="T"  # Draft 2D object (typed FeaturePython)
  FontFile = /System/Library/Fonts/Avenir Next Condensed.ttc
  Fuse = false
  Justification = 4
  JustificationReference = 0
  KeepLeftMargin = false
  MakeFace = true
  ObliqueAngle = 0
  Placement = pos=(2,187,19.01) rot=(0,0,1;4.71239rad)
  ScaleToSize = true
  Size = 28.5
  String = T
  Tracking = 0
  expr: Size = <<vars>>.font_size * 3
FEATURE [Part::Part2DObjectPython] ShapeString022  label="M"  # Draft 2D object (typed FeaturePython)
  FontFile = /System/Library/Fonts/Avenir Next Condensed.ttc
  Fuse = false
  Justification = 4
  JustificationReference = 0
  KeepLeftMargin = false
  MakeFace = true
  ObliqueAngle = 0
  Placement = pos=(-41,187,19.01) rot=(0,0,1;4.71239rad)
  ScaleToSize = true
  Size = 28.5
  String = M
  Tracking = 0
  expr: Size = <<vars>>.font_size * 3
FEATURE [Part::Part2DObjectPython] ShapeString023  label="A"  # Draft 2D object (typed FeaturePython)
  FontFile = /System/Library/Fonts/Avenir Next Condensed.ttc
  Fuse = false
  Justification = 4
  JustificationReference = 0
  KeepLeftMargin = false
  MakeFace = true
  ObliqueAngle = 0
  Placement = pos=(-75,187,19.01) rot=(0,0,1;4.71239rad)
  ScaleToSize = true
  Size = 28.5
  String = A
  Tracking = 0
  expr: Size = <<vars>>.font_size * 3
FEATURE [Part::Part2DObjectPython] ShapeString024  label="P2"  # Draft 2D object (typed FeaturePython)
  FontFile = /System/Library/Fonts/Avenir Next Condensed.ttc
  Fuse = false
  Justification = 4
  JustificationReference = 0
  KeepLeftMargin = false
  MakeFace = true
  ObliqueAngle = 0
  Placement = pos=(-109,186,19.01) rot=(0,0,1;4.71239rad)
  ScaleToSize = true
  Size = 28.5
  String = P
  Tracking = 0
  expr: Size = <<vars>>.font_size * 3
